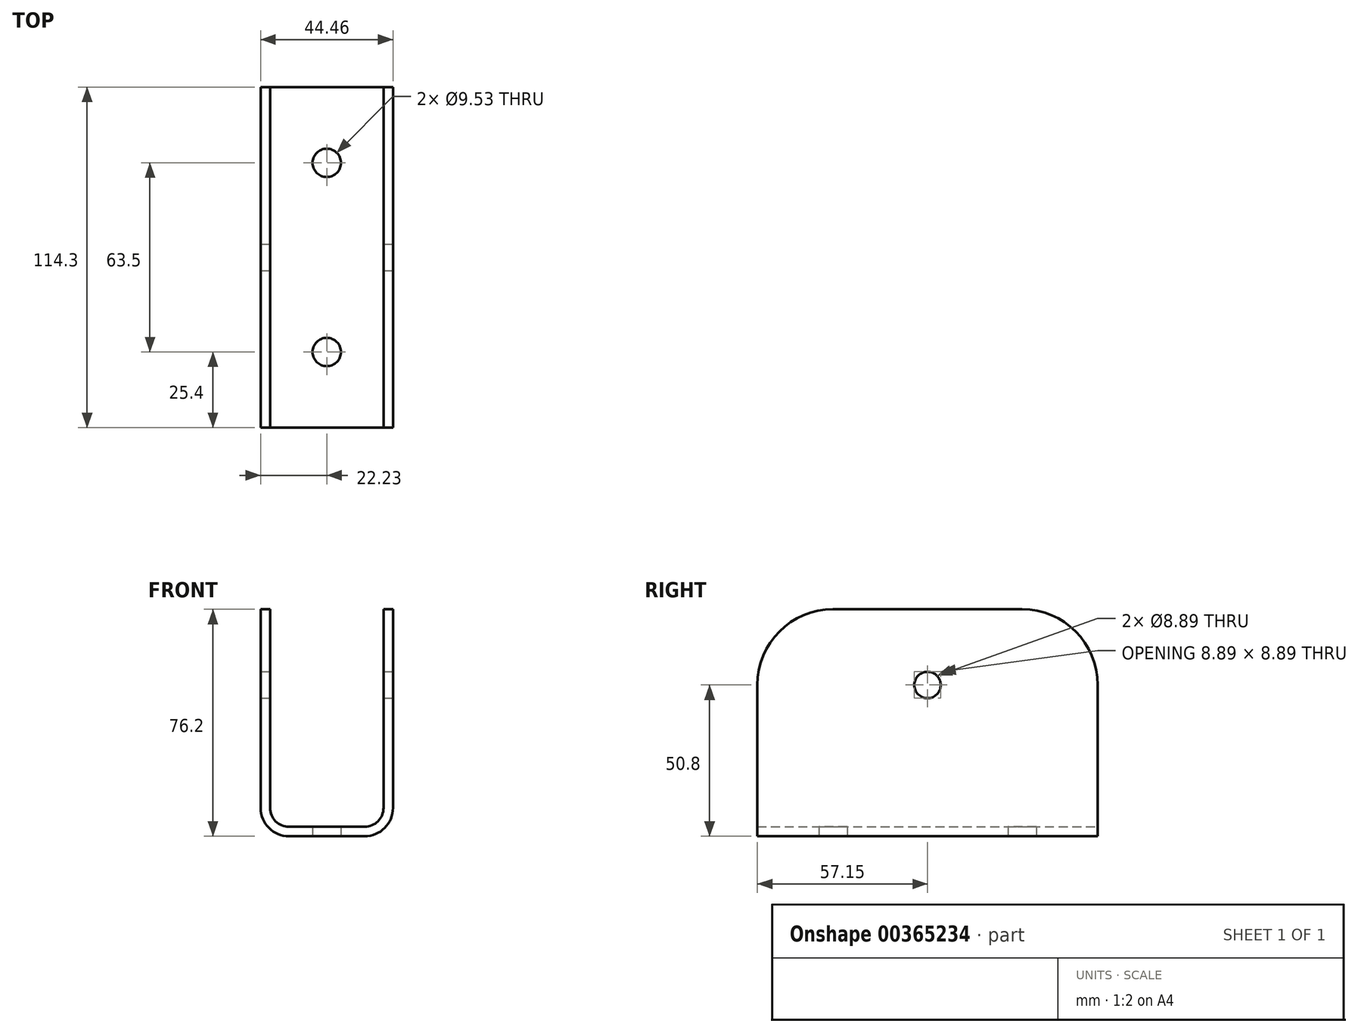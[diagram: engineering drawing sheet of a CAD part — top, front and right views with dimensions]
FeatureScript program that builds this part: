
annotation { "Feature Type Name" : "Feature", "Feature Type Description" : "" }
export const myFeature = defineFeature(function(context is Context, id is Id, definition is map)
    precondition{}
    {
        {
            var Q0;
            Q0=qCreatedBy(makeId("Front.planeOp"),FACE);
            var sketch = newSketch(context, id + "F0", { "sketchPlane" : qUnion([Q0])});
            skLineSegment(sketch, "E0", {"start": v(0, 0) * mm, "end": v(-22.22, 0) * mm});
            skLineSegment(sketch, "E1", {"start": v(-22.22, 0) * mm, "end": v(-22.23, 76.2) * mm});
            skLineSegment(sketch, "E2", {"start": v(-22.23, 76.2) * mm, "end": v(-19.05, 76.2) * mm});
            skLineSegment(sketch, "E3", {"start": v(-19.05, 76.2) * mm, "end": v(-19.05, 3.18) * mm});
            skLineSegment(sketch, "E4", {"start": v(-19.05, 3.18) * mm, "end": v(0, 3.18) * mm});
            skLineSegment(sketch, "E5", {"start": v(0, -36.54) * mm, "end": v(0, 73.22) * mm, "construction": true});
            skLineSegment(sketch, "E6.MirrorCS", {"start": v(22.23, 76.2) * mm, "end": v(19.05, 76.2) * mm});
            skLineSegment(sketch, "E7.MirrorCS", {"start": v(0, 0) * mm, "end": v(22.22, 0) * mm});
            skLineSegment(sketch, "E8.MirrorCS", {"start": v(19.05, 3.18) * mm, "end": v(0, 3.18) * mm});
            skLineSegment(sketch, "E9.MirrorCS", {"start": v(19.05, 76.2) * mm, "end": v(19.05, 3.18) * mm});
            skLineSegment(sketch, "E10.MirrorCS", {"start": v(22.22, 0) * mm, "end": v(22.23, 76.2) * mm});
            skSolve(sketch);
        }
        {
            var Q0;
            Q0 = qSketchRegion(id + "F0", true);
            extrude(context, id + "F1", {"entities" : qUnion([Q0]), "depth" : 57.15 * mm, "hasSecondDirection" : true, "secondDirectionOppositeDirection" : true, "secondDirectionDepth" : 57.15 * mm});
        }
        {
            var Q0;
            Q0=makeQuery(id+"F1.opExtrude","SWEPT_EDGE",EDGE,{"disambiguationData":[OSD([sQuery(id+"F0.wireOp",EDGE,"E8.MirrorCS"),sQuery(id+"F0.wireOp",EDGE,"E9.MirrorCS")])]});
            fillet(context, id + "F2", {"entities" : qUnion([Q0]), "radius" : 6.35 * mm, "tangentPropagation" : true, "allowEdgeOverflow" : false});
        }
        {
            var Q0;
            Q0=makeQuery(id+"F1.opExtrude","SWEPT_EDGE",EDGE,{"disambiguationData":[OSD([sQuery(id+"F0.wireOp",EDGE,"E3"),sQuery(id+"F0.wireOp",EDGE,"E4")])]});
            fillet(context, id + "F3", {"entities" : qUnion([Q0]), "radius" : 6.35 * mm, "tangentPropagation" : true, "allowEdgeOverflow" : false});
        }
        {
            var Q0;
            Q0=makeQuery(id+"F1.opExtrude","SWEPT_EDGE",EDGE,{"disambiguationData":[OSD([sQuery(id+"F0.wireOp",EDGE,"E7.MirrorCS"),sQuery(id+"F0.wireOp",EDGE,"E10.MirrorCS")])]});
            var Q1;
            Q1=makeQuery(id+"F1.opExtrude","SWEPT_EDGE",EDGE,{"disambiguationData":[OSD([sQuery(id+"F0.wireOp",EDGE,"E0"),sQuery(id+"F0.wireOp",EDGE,"E1")])]});
            fillet(context, id + "F4", {"entities" : qUnion([Q0, Q1]), "radius" : 9.52 * mm, "tangentPropagation" : true, "allowEdgeOverflow" : false});
        }
        {
            var Q0;
            Q0=makeQuery(id+"F1.opExtrude","SWEPT_FACE",FACE,{"disambiguationData":[OSD([sQuery(id+"F0.wireOp",EDGE,"E1")])]});
            var sketch = newSketch(context, id + "F5", { "sketchPlane" : qUnion([Q0])});
            skCircle(sketch, "E11", {"center": v(0, 50.8) * mm, "radius": 4.45 * mm});
            skSolve(sketch);
        }
        {
            var Q0;
            Q0 = qSketchRegion(id + "F5", true);
            extrude(context, id + "F6", {"entities" : qUnion([Q0]), "operationType" : NewBodyOperationType.REMOVE, "depth" : 101.35 * mm, "hasSecondDirection" : true, "secondDirectionOppositeDirection" : true, "secondDirectionDepth" : 150.62 * mm});
        }
        {
            var Q0;
            Q0=makeQuery(id+"F1.opExtrude","SWEPT_FACE",FACE,{"disambiguationData":[OSD([sQuery(id+"F0.wireOp",EDGE,"E4"),sQuery(id+"F0.wireOp",EDGE,"E8.MirrorCS")])]});
            var sketch = newSketch(context, id + "F7", { "sketchPlane" : qUnion([Q0])});
            skCircle(sketch, "E12", {"center": v(0, 31.75) * mm, "radius": 4.76 * mm});
            skCircle(sketch, "E13.MirrorC", {"center": v(0, -31.75) * mm, "radius": 4.76 * mm});
            skSolve(sketch);
        }
        {
            var Q0;
            Q0 = qSketchRegion(id + "F7", true);
            extrude(context, id + "F8", {"entities" : qUnion([Q0]), "operationType" : NewBodyOperationType.REMOVE, "depth" : 25.4 * mm, "hasSecondDirection" : true, "secondDirectionOppositeDirection" : true, "secondDirectionDepth" : 25.4 * mm});
        }
        {
            var Q0;
            Q0=makeQuery(id+"F1.opExtrude","CAP_EDGE",EDGE,{"disambiguationData":[OSD([sQuery(id+"F0.wireOp",EDGE,"E6.MirrorCS")])],"isStart":true});
            var Q1;
            Q1=makeQuery(id+"F1.opExtrude","CAP_EDGE",EDGE,{"disambiguationData":[OSD([sQuery(id+"F0.wireOp",EDGE,"E2")])],"isStart":true});
            var Q2;
            Q2=makeQuery(id+"F1.opExtrude","CAP_EDGE",EDGE,{"disambiguationData":[OSD([sQuery(id+"F0.wireOp",EDGE,"E6.MirrorCS")])],"isStart":false});
            var Q3;
            Q3=makeQuery(id+"F1.opExtrude","CAP_EDGE",EDGE,{"disambiguationData":[OSD([sQuery(id+"F0.wireOp",EDGE,"E2")])],"isStart":false});
            fillet(context, id + "F9", {"entities" : qUnion([Q0, Q1, Q2, Q3]), "radius" : 25.4 * mm, "tangentPropagation" : true, "allowEdgeOverflow" : false});
        }
    });
